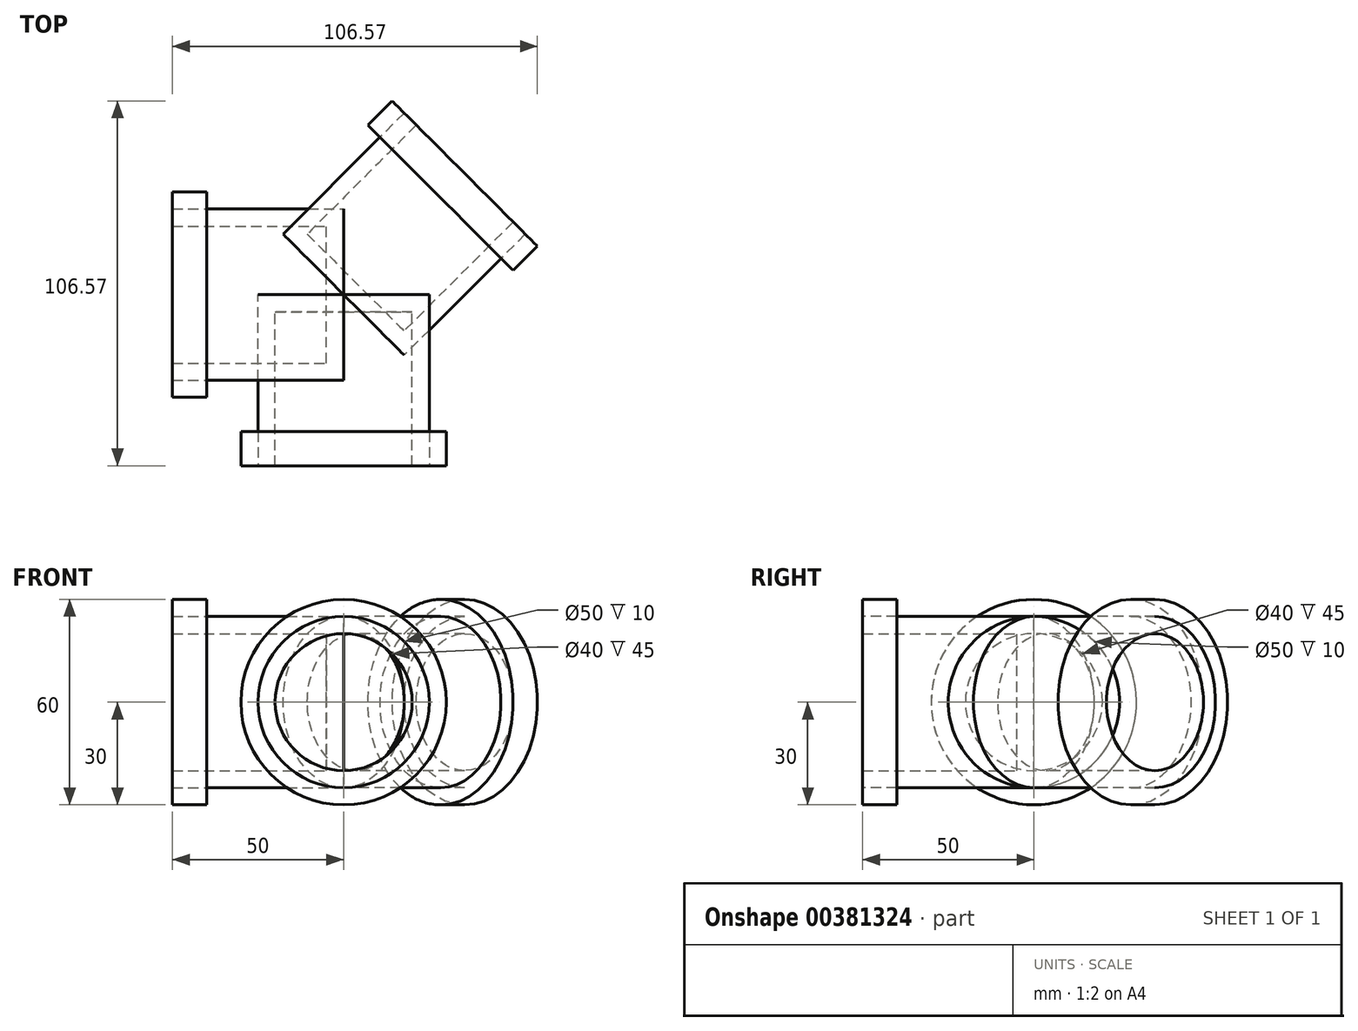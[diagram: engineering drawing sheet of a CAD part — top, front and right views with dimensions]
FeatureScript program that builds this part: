
annotation { "Feature Type Name" : "Feature", "Feature Type Description" : "" }
export const myFeature = defineFeature(function(context is Context, id is Id, definition is map)
    precondition{}
    {
        {
            var Q0;
            Q0=qCreatedBy(makeId("Front.planeOp"),FACE);
            var sketch = newSketch(context, id + "F0", { "sketchPlane" : qUnion([Q0])});
            skCircle(sketch, "E0", {"center": v(0, 0) * mm, "radius": 25 * mm});
            skSolve(sketch);
        }
        {
            var Q0;
            Q0=makeQuery(id+"F0.imprint","IMPRINT",FACE,{"disambiguationData":[TD([[makeQuery(id+"F0.imprint","IMPRINT",EDGE,{"derivedFrom":sQuery(id+"F0.wireOp",EDGE,"E0")}),1.0]])]});
            extrude(context, id + "F1", {"entities" : qUnion([Q0]), "depth" : 50 * mm});
        }
        {
            var Q0;
            Q0=qCreatedBy(makeId("Right.planeOp"),FACE);
            var sketch = newSketch(context, id + "F2", { "sketchPlane" : qUnion([Q0])});
            skLineSegment(sketch, "E1", {"start": v(0, 0) * mm, "end": v(0, 69.61) * mm, "construction": true});
            skSolve(sketch);
        }
        {
            var Q0;
            Q0=makeQuery(id+"F1.opExtrude","SWEPT_BODY",BODY,{"disambiguationData":[OSD([sQuery(id+"F0.wireOp",EDGE,"E0")])]});
            var Q1;
            Q1=sQuery(id+"F2.wireOp",EDGE,"E1");
            transform(context, id + "F3", {"entities" : qUnion([Q0]), "transformType" : TransformType.ROTATION, "transformAxis" : qUnion([Q1]), "angle" : 135 * degree, "makeCopy" : true});
        }
        {
            var Q0;
            Q0=makeQuery(id+"F3.opPattern","COPY",BODY,{"derivedFrom":makeQuery(id+"F1.opExtrude","SWEPT_BODY",BODY,{"disambiguationData":[OSD([sQuery(id+"F0.wireOp",EDGE,"E0")])]}),"instanceName":"1"});
            var Q1;
            Q1=sQuery(id+"F2.wireOp",EDGE,"E1");
            transform(context, id + "F4", {"entities" : qUnion([Q0]), "transformType" : TransformType.ROTATION, "transformAxis" : qUnion([Q1]), "angle" : 135 * degree, "makeCopy" : true});
        }
        {
            var Q0;
            Q0=makeQuery(id+"F4.opPattern","COPY",FACE,{"derivedFrom":makeQuery(id+"F3.opPattern","COPY",FACE,{"derivedFrom":makeQuery(id+"F1.opExtrude","CAP_FACE",FACE,{"disambiguationData":[OSD([sQuery(id+"F0.wireOp",EDGE,"E0")])],"isStart":false}),"instanceName":"1"}),"instanceName":"1"});
            var Q1;
            Q1=makeQuery(id+"F1.opExtrude","CAP_FACE",FACE,{"disambiguationData":[OSD([sQuery(id+"F0.wireOp",EDGE,"E0")])],"isStart":false});
            var Q2;
            Q2=makeQuery(id+"F3.opPattern","COPY",FACE,{"derivedFrom":makeQuery(id+"F1.opExtrude","CAP_FACE",FACE,{"disambiguationData":[OSD([sQuery(id+"F0.wireOp",EDGE,"E0")])],"isStart":false}),"instanceName":"1"});
            shell(context, id + "F5", {"entities" : qUnion([Q0, Q1, Q2]), "thickness" : 5 * mm});
        }
        {
            var Q0;
            Q0=makeQuery(id+"F1.opExtrude","CAP_FACE",FACE,{"disambiguationData":[OSD([sQuery(id+"F0.wireOp",EDGE,"E0")])],"isStart":false});
            var sketch = newSketch(context, id + "F6", { "sketchPlane" : qUnion([Q0])});
            skCircle(sketch, "E2", {"center": v(0, 0) * mm, "radius": 30 * mm});
            skCircle(sketch, "E3", {"center": v(0, 0) * mm, "radius": 25 * mm});
            skSolve(sketch);
        }
        {
            var Q0;
            Q0=makeQuery(id+"F6.imprint","IMPRINT",FACE,{"disambiguationData":[TD([[makeQuery(id+"F6.imprint","IMPRINT",EDGE,{"derivedFrom":sQuery(id+"F6.wireOp",EDGE,"E2")}),1.0]])]});
            extrude(context, id + "F7", {"entities" : qUnion([Q0]), "oppositeDirection" : true, "depth" : 10 * mm});
        }
        {
            var Q0;
            Q0=makeQuery(id+"F7.opExtrude","SWEPT_BODY",BODY,{"disambiguationData":[OSD([sQuery(id+"F6.wireOp",EDGE,"E2"),sQuery(id+"F6.wireOp",EDGE,"E3")])]});
            var Q1;
            Q1=sQuery(id+"F2.wireOp",EDGE,"E1");
            transform(context, id + "F8", {"entities" : qUnion([Q0]), "transformType" : TransformType.ROTATION, "transformAxis" : qUnion([Q1]), "angle" : 135 * degree, "makeCopy" : true});
        }
        {
            var Q0;
            Q0=makeQuery(id+"F8.opPattern","COPY",BODY,{"derivedFrom":makeQuery(id+"F7.opExtrude","SWEPT_BODY",BODY,{"disambiguationData":[OSD([sQuery(id+"F6.wireOp",EDGE,"E2"),sQuery(id+"F6.wireOp",EDGE,"E3")])]}),"instanceName":"1"});
            var Q1;
            Q1=sQuery(id+"F2.wireOp",EDGE,"E1");
            transform(context, id + "F9", {"entities" : qUnion([Q0]), "transformType" : TransformType.ROTATION, "transformAxis" : qUnion([Q1]), "angle" : 135 * degree, "makeCopy" : true});
        }
    });
